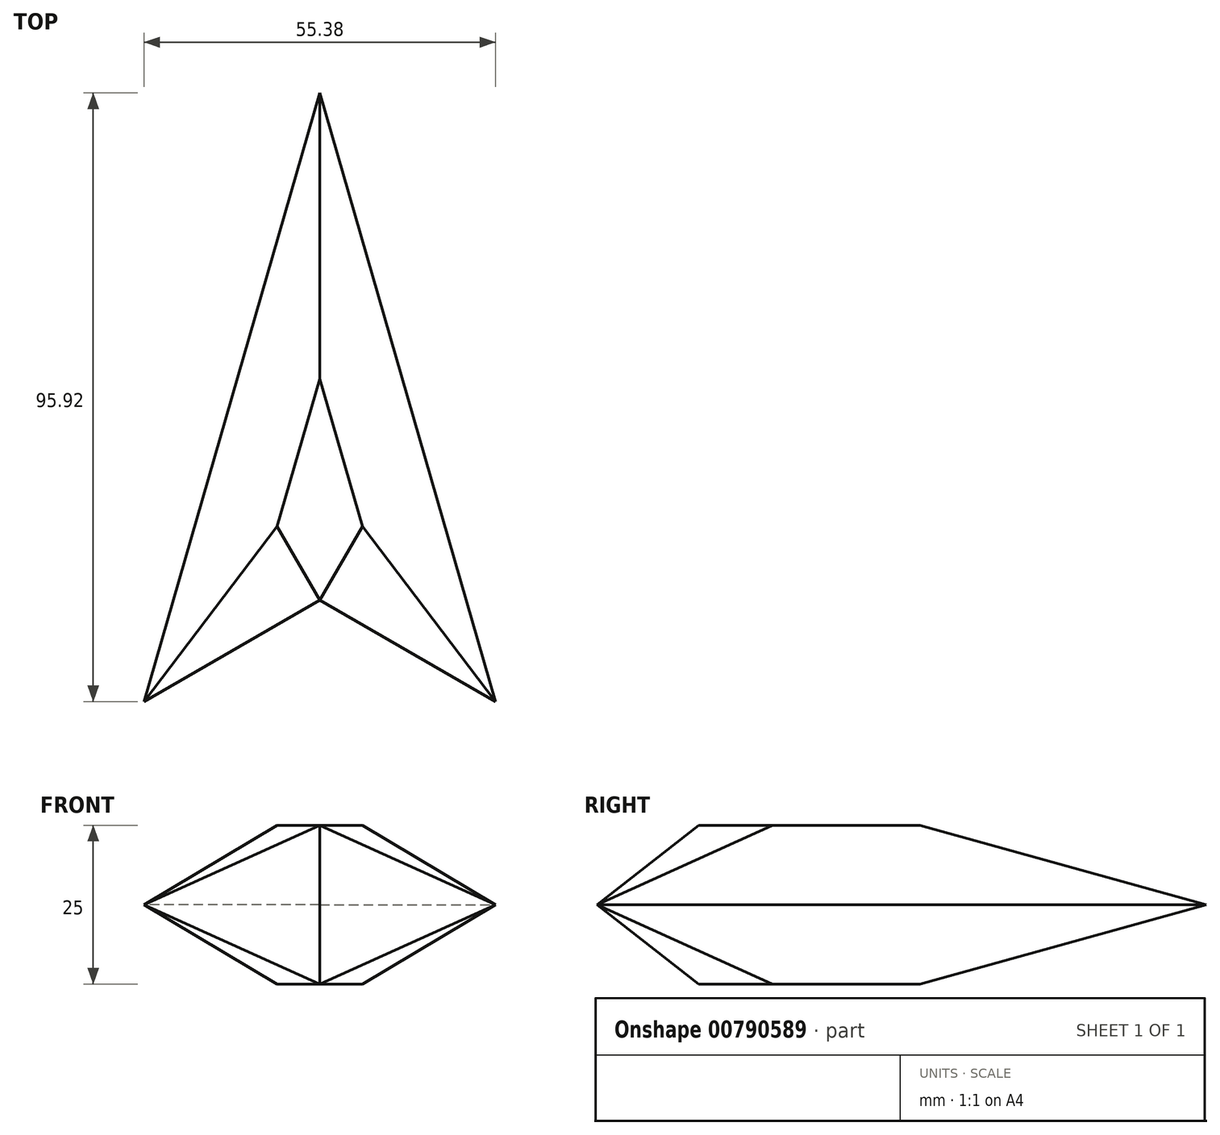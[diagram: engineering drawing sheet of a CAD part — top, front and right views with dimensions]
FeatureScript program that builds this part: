
annotation { "Feature Type Name" : "Feature", "Feature Type Description" : "" }
export const myFeature = defineFeature(function(context is Context, id is Id, definition is map)
    precondition{}
    {
        {
            var Q0;
            Q0=qCreatedBy(makeId("Top.planeOp"),FACE);
            var sketch = newSketch(context, id + "F0", { "sketchPlane" : qUnion([Q0])});
            skLineSegment(sketch, "E0", {"start": v(0, 0) * mm, "end": v(0, -30) * mm, "construction": true});
            skLineSegment(sketch, "E1", {"start": v(0, 0) * mm, "end": v(8.66, -5) * mm});
            skLineSegment(sketch, "E2", {"start": v(0, 25) * mm, "end": v(8.66, -5) * mm});
            skLineSegment(sketch, "E3", {"start": v(0, 0) * mm, "end": v(0, 25) * mm});
            skLineSegment(sketch, "E4.MirrorCS", {"start": v(0, 25) * mm, "end": v(-8.66, -5) * mm});
            skLineSegment(sketch, "E5.MirrorCS", {"start": v(0, 0) * mm, "end": v(-8.66, -5) * mm});
            skSolve(sketch);
        }
        {
            var Q0;
            Q0=makeQuery(id+"F0.imprint","IMPRINT",FACE,{"disambiguationData":[TD([[makeQuery(id+"F0.imprint","IMPRINT",EDGE,{"derivedFrom":sQuery(id+"F0.wireOp",EDGE,"E3")}),1.0]])]});
            extrude(context, id + "F1", {"entities" : qUnion([Q0]), "endBound" : BoundingType.SYMMETRIC, "depth" : 5 * mm, "offsetDistance" : 25 * mm});
        }
        {
            var Q0;
            Q0=makeQuery(id+"F1.opExtrude","CAP_EDGE",EDGE,{"disambiguationData":[OSD([sQuery(id+"F0.wireOp",EDGE,"E4.MirrorCS")])],"isStart":false});
            var Q1;
            Q1=makeQuery(id+"F1.opExtrude","CAP_EDGE",EDGE,{"disambiguationData":[OSD([sQuery(id+"F0.wireOp",EDGE,"E4.MirrorCS")])],"isStart":true});
            chamfer(context, id + "F2", {"entities" : qUnion([Q0, Q1]), "width" : 5 * mm, "tangentPropagation" : true});
        }
        {
            var Q0;
            Q0=makeQuery(id+"F1.opExtrude","SWEPT_FACE",FACE,{"disambiguationData":[OSD([sQuery(id+"F0.wireOp",EDGE,"E5.MirrorCS")])]});
            var sketch = newSketch(context, id + "F3", { "sketchPlane" : qUnion([Q0])});
            skLineSegment(sketch, "E6", {"start": v(-6.4, 0) * mm, "end": v(0, 2.5) * mm});
            skLineSegment(sketch, "E7", {"start": v(-6.4, 0) * mm, "end": v(0, -2.5) * mm});
            skSolve(sketch);
        }
        {
            var Q0;
            Q0=makeQuery(id+"F3.imprint","IMPRINT",FACE,{"disambiguationData":[TD([[makeQuery(id+"F3.imprint","IMPRINT",EDGE,{"derivedFrom":sQuery(id+"F3.wireOp",EDGE,"E7")}),-1.0]])]});
            var Q1;
            Q1=makeQuery(id+"F3.imprint","IMPRINT",FACE,{"disambiguationData":[TD([[makeQuery(id+"F3.imprint","IMPRINT",EDGE,{"derivedFrom":sQuery(id+"F3.wireOp",EDGE,"E6")}),1.0]])]});
            extrude(context, id + "F4", {"entities" : qUnion([Q0, Q1]), "operationType" : NewBodyOperationType.REMOVE, "oppositeDirection" : true, "depth" : 25 * mm, "offsetDistance" : 25 * mm});
        }
        {
            var Q0;
            Q0=makeQuery(id+"F1.opExtrude","SWEPT_BODY",BODY,{"disambiguationData":[OSD([sQuery(id+"F0.wireOp",EDGE,"E3"),sQuery(id+"F0.wireOp",EDGE,"E4.MirrorCS"),sQuery(id+"F0.wireOp",EDGE,"E5.MirrorCS")])]});
            var Q1;
            Q1=qCreatedBy(makeId("Right.planeOp"),FACE);
            mirror(context, id + "F5", {"operationType" : NewBodyOperationType.ADD, "entities" : qUnion([Q0]), "mirrorPlane" : qUnion([Q1])});
        }
        {
            var Q0;
            Q0=qCreatedBy(makeId("Front.planeOp"),FACE);
            var sketch = newSketch(context, id + "F6", { "sketchPlane" : qUnion([Q0])});
            skCircle(sketch, "E8", {"center": v(0, 0) * mm, "radius": 12.5 * mm});
            skSolve(sketch);
        }
        {
            var Q0;
            Q0=makeQuery(id+"F1.opExtrude","SWEPT_BODY",BODY,{"disambiguationData":[OSD([sQuery(id+"F0.wireOp",EDGE,"E3"),sQuery(id+"F0.wireOp",EDGE,"E4.MirrorCS"),sQuery(id+"F0.wireOp",EDGE,"E5.MirrorCS")])]});
            var Q1;
            Q1=sQuery(id+"F6.wireOp",VERTEX,"E8.center");
            transform(context, id + "F7", {"entities" : qUnion([Q0]), "transformType" : TransformType.SCALE_UNIFORMLY, "scale" : 5, "scalePoint" : qUnion([Q1]), "makeCopy" : false});
        }
    });
